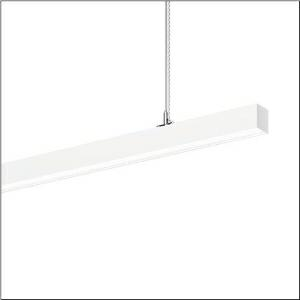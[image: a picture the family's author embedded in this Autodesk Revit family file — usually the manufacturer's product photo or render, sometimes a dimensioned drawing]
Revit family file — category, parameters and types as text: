
# Revit family: silica_r__21_51mx33da37wb_a2a9
name_source: partatom
category: Lighting Fixtures
units: mm (PartAtom-declared; Revit-internal decimal feet)

## family parameters
Cut with Voids When Loaded = No
Host = Face
Light Source = No
Part Type = Normal
Room Calculation Point = No
Round Connector Dimension = Use Diameter
Shared = No

## types (1)
- --- (1 x LED, 5910 lm, 41.3 W, 3000K)
    Apparent Load = 41 VA
    CIE Flux Codes = 78 96 99 55 100
    Color Rendering = 80
    Color Temperature = 3000K
    Default Elevation = 1800 mm
    Description = Silica® 21, office luminaire, primary optical cover: prismatic diffuser, of PMMA, CAT 2 (L<= 3000cd/m²), light emission: direct/indirect distribution, primary light characteristic: symmetric, installation type: suspended mounting, LED, rated luminous flux: 5.910lm, luminous efficacy: 143lm/W, light colour: 830, colour temperature: 3000K, control gear: DALI 2, with terminal, 3+2-pole, max. 2.5mm², mains connection: 220..240V, AC, 50/60Hz, rated input power: 41.3W, luminaire housing, of aluminium, traffic white (RAL 9016), length: 1.204mm, width: 53mm, height: 53mm, protection rating (complete): IP20, insulation class (complete): insulation class I (protective earthing), certification: CE, permissible operating ambient temperature: 0..+35°C, standard: EN 50419, packaging unit: 1 piece
    Height = 53 mm
    Lamp = 1 x LED
    Lamp Light Flux = 5910 lm
    Lamp Power = 41.3 W
    Lamp count = 1
    Length = 1204 mm
    Luminous efficacy = 143 lm/W
    Manufacturer = Siteco
    ModVariant = No
    Model = 51MX33DA37WB
    Mounting Place = Ceiling
    Mounting Type = Pendant
    Number of Poles = 1
    OnlyDefault = Yes
    Power Factor = 1
    Product Name = Silica® 21
    Product group = office luminaire | ceiling pendant
    ProductGroupID = 904
    Protection Class = Protection class I
    Protection Degree = IP 20
    RLX_Detail_Level = 1
    RLX_Emergency_Light_Flux = 0 lm
    RLX_Emergency_Type = 0
    RLX_Emergency_Type_DB = No
    RlxData = <blob elided: 21529 chars, md5=285e1871>
    Socket = socket
    Standby Power = 0 W
    System Light Flux = 5910 lm
    System Power = 41 W
    Type Comments = factory setting: luminous flux: 100 % | dim-lin: 254 | 345 mA
    Type Image = l_1349007.jpg
    URL = http://relux.com
    VarID = @adj_118878
    Voltage = 0 V
    Weight = 0.00 kg
    Width = 53 mm

## geometry (parser evidence)
native form markers: Blend x4, Sweep x15
no freeform markers — native parametric forms only
